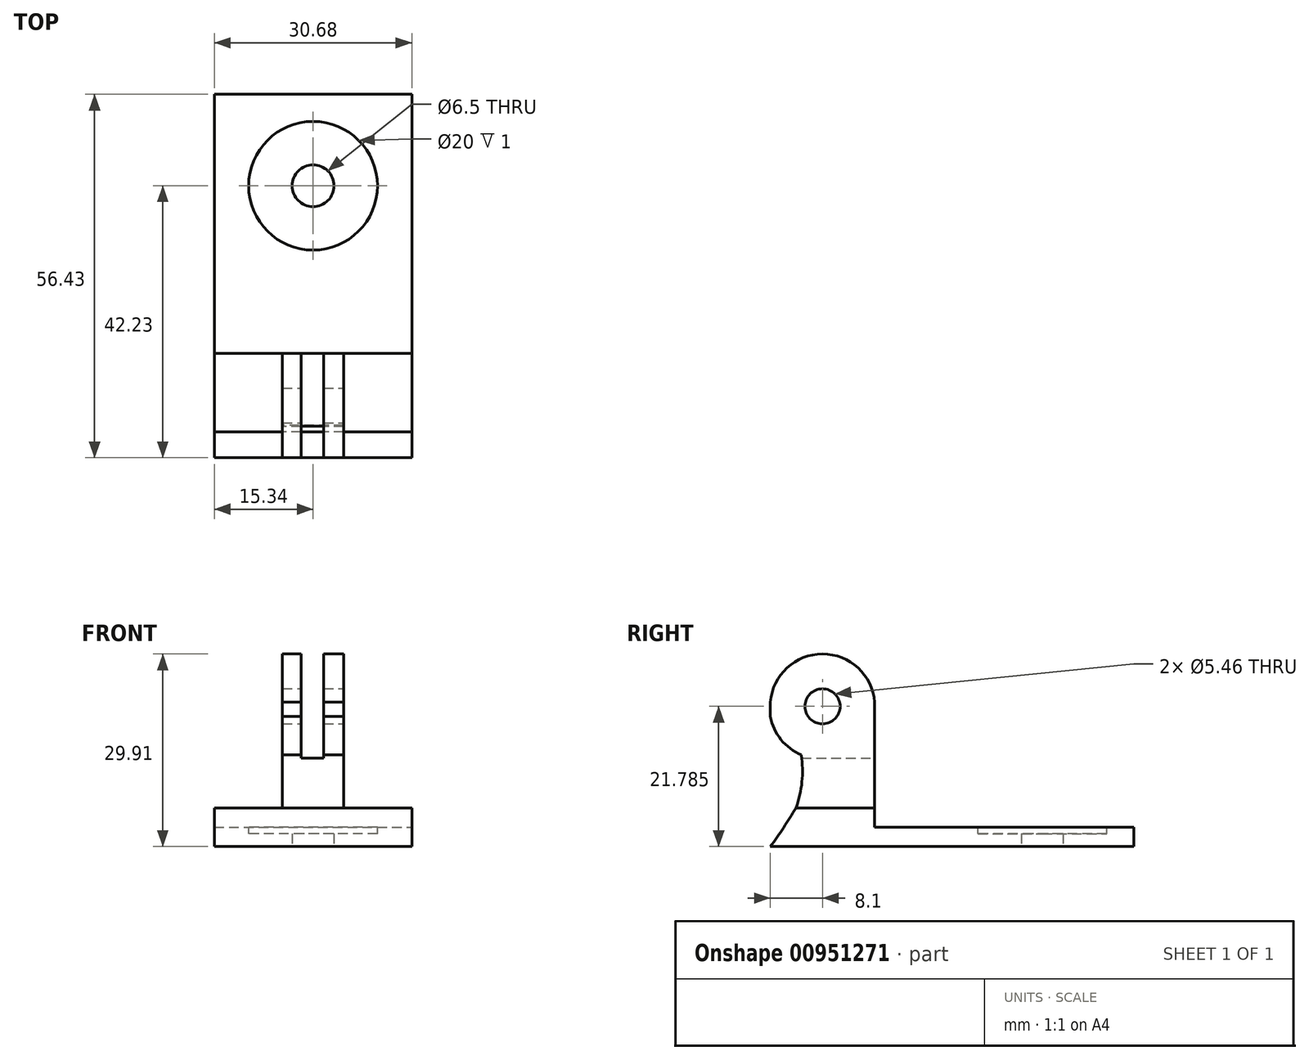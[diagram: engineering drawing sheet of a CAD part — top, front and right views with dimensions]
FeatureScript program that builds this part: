
annotation { "Feature Type Name" : "Feature", "Feature Type Description" : "" }
export const myFeature = defineFeature(function(context is Context, id is Id, definition is map)
    precondition{}
    {
        {
            var Q0;
            Q0=qCreatedBy(makeId("Top.planeOp"),FACE);
            var sketch = newSketch(context, id + "F0", { "sketchPlane" : qUnion([Q0])});
            skLineSegment(sketch, "E0.bottom", {"start": v(-15.34, 42.23) * mm, "end": v(15.34, 42.23) * mm});
            skLineSegment(sketch, "E0.top", {"start": v(-15.34, -42.23) * mm, "end": v(15.34, -42.23) * mm});
            skLineSegment(sketch, "E0.left", {"start": v(-15.34, 42.23) * mm, "end": v(-15.34, -42.23) * mm});
            skLineSegment(sketch, "E0.right", {"start": v(15.34, 42.23) * mm, "end": v(15.34, -42.23) * mm});
            skPoint(sketch, "E0.middle", {"position": v(0, 0) * mm});
            skCircle(sketch, "E1", {"center": v(0, 0) * mm, "radius": 3.25 * mm});
            skSolve(sketch);
        }
        {
            var Q0;
            Q0=makeQuery(id+"F0.imprint","IMPRINT",FACE,{"disambiguationData":[TD([[makeQuery(id+"F0.imprint","IMPRINT",EDGE,{"derivedFrom":sQuery(id+"F0.wireOp",EDGE,"E0.bottom")}),-1.0]])]});
            extrude(context, id + "F1", {"entities" : qUnion([Q0]), "depth" : 3 * mm, "offsetDistance" : 25 * mm});
        }
        {
            var Q0;
            Q0=makeQuery(id+"F1.opExtrude","CAP_FACE",FACE,{"disambiguationData":[OSD([sQuery(id+"F0.wireOp",EDGE,"E0.bottom"),sQuery(id+"F0.wireOp",EDGE,"E0.top"),sQuery(id+"F0.wireOp",EDGE,"E0.left"),sQuery(id+"F0.wireOp",EDGE,"E0.right"),sQuery(id+"F0.wireOp",EDGE,"E1")])],"isStart":false});
            var sketch = newSketch(context, id + "F2", { "sketchPlane" : qUnion([Q0])});
            skLineSegment(sketch, "E2.bottom", {"start": v(-15.34, -26.03) * mm, "end": v(15.34, -26.03) * mm});
            skLineSegment(sketch, "E2.top", {"start": v(-15.34, -42.23) * mm, "end": v(15.34, -42.23) * mm});
            skLineSegment(sketch, "E2.left", {"start": v(-15.34, -26.03) * mm, "end": v(-15.34, -42.23) * mm});
            skLineSegment(sketch, "E2.right", {"start": v(15.34, -26.03) * mm, "end": v(15.34, -42.23) * mm});
            skSolve(sketch);
        }
        {
            var Q0;
            Q0 = qSketchRegion(id + "F2", true);
            extrude(context, id + "F3", {"entities" : qUnion([Q0]), "operationType" : NewBodyOperationType.ADD, "depth" : 3 * mm, "offsetDistance" : 25 * mm});
        }
        {
            var Q0;
            Q0=makeQuery(id+"F3.opExtrude","CAP_FACE",FACE,{"disambiguationData":[OSD([sQuery(id+"F2.wireOp",EDGE,"E2.bottom"),sQuery(id+"F2.wireOp",EDGE,"E2.top"),sQuery(id+"F2.wireOp",EDGE,"E2.left"),sQuery(id+"F2.wireOp",EDGE,"E2.right")])],"isStart":false});
            var sketch = newSketch(context, id + "F4", { "sketchPlane" : qUnion([Q0])});
            skLineSegment(sketch, "E3.bottom", {"start": v(4.75, -42.23) * mm, "end": v(-4.75, -42.23) * mm});
            skLineSegment(sketch, "E3.top", {"start": v(4.75, 42.23) * mm, "end": v(-4.75, 42.23) * mm});
            skLineSegment(sketch, "E3.left", {"start": v(4.75, -42.23) * mm, "end": v(4.75, 42.23) * mm});
            skLineSegment(sketch, "E3.right", {"start": v(-4.75, -42.23) * mm, "end": v(-4.75, 42.23) * mm});
            skPoint(sketch, "E3.middle", {"position": v(0, 0) * mm});
            skLineSegment(sketch, "E4", {"start": v(-4.75, -26.03) * mm, "end": v(4.75, -26.03) * mm});
            skLineSegment(sketch, "E5", {"start": v(4.75, -26.03) * mm, "end": v(4.75, -42.23) * mm});
            skLineSegment(sketch, "E6", {"start": v(-4.75, -42.23) * mm, "end": v(-4.75, -26.03) * mm});
            skSolve(sketch);
        }
        {
            var Q0;
            {var subQ0=sQuery(id+"F4.wireOp",EDGE,"E3.bottom");Q0=makeQuery(id+"F4.imprint","IMPRINT",FACE,{"disambiguationData":[TD([[makeQuery(id+"F4.imprint","IMPRINT",EDGE,{"derivedFrom":subQ0}),1.0]])]});}
            extrude(context, id + "F5", {"entities" : qUnion([Q0]), "operationType" : NewBodyOperationType.ADD, "depth" : 24 * mm, "offsetDistance" : 25 * mm});
        }
        {
            var Q0;
            Q0=makeQuery(id+"F5.boolean.opBoolean","MERGE",FACE,{"derivedFrom":[makeQuery(id+"F3.opExtrude","SWEPT_FACE",FACE,{"disambiguationData":[OSD([sQuery(id+"F2.wireOp",EDGE,"E2.bottom")])]}),makeQuery(id+"F5.opExtrude","SWEPT_FACE",FACE,{"disambiguationData":[OSD([sQuery(id+"F4.wireOp",EDGE,"E4")])]})]});
            var sketch = newSketch(context, id + "F6", { "sketchPlane" : qUnion([Q0])});
            skLineSegment(sketch, "E7.bottom", {"start": v(-1.65, 30) * mm, "end": v(1.85, 30) * mm});
            skLineSegment(sketch, "E7.top", {"start": v(-1.65, 13.75) * mm, "end": v(1.85, 13.75) * mm});
            skLineSegment(sketch, "E7.left", {"start": v(-1.65, 30) * mm, "end": v(-1.65, 13.75) * mm});
            skLineSegment(sketch, "E7.right", {"start": v(1.85, 30) * mm, "end": v(1.85, 13.75) * mm});
            skSolve(sketch);
        }
        {
            var Q0;
            Q0=makeQuery(id+"F6.imprint","IMPRINT",FACE,{"disambiguationData":[TD([[makeQuery(id+"F6.imprint","IMPRINT",EDGE,{"derivedFrom":sQuery(id+"F6.wireOp",EDGE,"E7.bottom")}),1.0]])]});
            extrude(context, id + "F7", {"entities" : qUnion([Q0]), "operationType" : NewBodyOperationType.REMOVE, "oppositeDirection" : true, "depth" : 18 * mm, "offsetDistance" : 25 * mm});
        }
        {
            var Q0;
            Q0=makeQuery(id+"F5.opExtrude","SWEPT_FACE",FACE,{"disambiguationData":[OSD([sQuery(id+"F4.wireOp",EDGE,"E3.left")])]});
            var sketch = newSketch(context, id + "F8", { "sketchPlane" : qUnion([Q0])});
            skLineSegment(sketch, "E8", {"start": v(-34.13, 30) * mm, "end": v(-34.13, 21.78) * mm});
            skCircle(sketch, "E9", {"center": v(-34.13, 21.78) * mm, "radius": 8.13 * mm});
            skCircle(sketch, "E10", {"center": v(-34.13, 21.78) * mm, "radius": 2.73 * mm});
            skLineSegment(sketch, "E11", {"start": v(-42.23, 18) * mm, "end": v(-42.23, 30) * mm});
            skLineSegment(sketch, "E12", {"start": v(-42.23, 30) * mm, "end": v(-34.13, 30) * mm});
            skLineSegment(sketch, "E13", {"start": v(-26.03, 30) * mm, "end": v(-26.03, 22.44) * mm});
            skSolve(sketch);
        }
        {
            var Q0;
            {var subQ0=sQuery(id+"F8.wireOp",EDGE,"E12");var subQ1=sQuery(id+"F8.wireOp",EDGE,"E9");var subQ2=makeQuery(id+"F8.imprint","INTERSECT",VERTEX,{"derivedFrom":[subQ1,subQ0]});Q0=makeQuery(id+"F8.imprint","IMPRINT",FACE,{"disambiguationData":[TD([[makeQuery(id+"F8.imprint","IMPRINT",EDGE,{"disambiguationData":[TD([[subQ2,-1.0]])],"derivedFrom":subQ1}),-1.0]])]});}
            var Q1;
            {var subQ0=sQuery(id+"F8.wireOp",EDGE,"E13");Q1=makeQuery(id+"F8.imprint","IMPRINT",FACE,{"disambiguationData":[TD([[makeQuery(id+"F8.imprint","IMPRINT",EDGE,{"derivedFrom":subQ0}),-1.0]])]});}
            var Q2;
            Q2=makeQuery(id+"F8.imprint","IMPRINT",FACE,{"disambiguationData":[TD([[makeQuery(id+"F8.imprint","IMPRINT",EDGE,{"derivedFrom":sQuery(id+"F8.wireOp",EDGE,"E10")}),1.0]])]});
            extrude(context, id + "F9", {"entities" : qUnion([Q0, Q1, Q2]), "operationType" : NewBodyOperationType.REMOVE, "oppositeDirection" : true, "depth" : 10 * mm, "offsetDistance" : 25 * mm});
        }
        {
            var Q0;
            Q0=makeQuery(id+"F1.opExtrude","CAP_FACE",FACE,{"disambiguationData":[OSD([sQuery(id+"F0.wireOp",EDGE,"E0.bottom"),sQuery(id+"F0.wireOp",EDGE,"E0.top"),sQuery(id+"F0.wireOp",EDGE,"E0.left"),sQuery(id+"F0.wireOp",EDGE,"E0.right"),sQuery(id+"F0.wireOp",EDGE,"E1")])],"isStart":false});
            var sketch = newSketch(context, id + "F10", { "sketchPlane" : qUnion([Q0])});
            skCircle(sketch, "E14", {"center": v(0, 0) * mm, "radius": 10 * mm});
            skCircle(sketch, "E15", {"center": v(0, 0) * mm, "radius": 2.85 * mm});
            skSolve(sketch);
        }
        {
            var Q0;
            Q0=makeQuery(id+"F10.imprint","IMPRINT",FACE,{"disambiguationData":[TD([[makeQuery(id+"F10.imprint","IMPRINT",EDGE,{"derivedFrom":sQuery(id+"F10.wireOp",EDGE,"E14")}),1.0]])]});
            extrude(context, id + "F11", {"entities" : qUnion([Q0]), "operationType" : NewBodyOperationType.REMOVE, "oppositeDirection" : true, "depth" : 1 * mm, "offsetDistance" : 25 * mm});
        }
        {
            var Q0;
            {var subQ0=sQuery(id+"F0.wireOp",EDGE,"E0.left");var subQ1=sQuery(id+"F0.wireOp",EDGE,"E0.right");var subQ2=sQuery(id+"F0.wireOp",EDGE,"E0.bottom");Q0=makeQuery(id+"F11.boolean.opBoolean","SPLIT",FACE,{"disambiguationData":[TD([makeQuery(id+"F1.opExtrude","SWEPT_FACE",FACE,{"disambiguationData":[OSD([subQ2])]})])],"derivedFrom":makeQuery(id+"F1.opExtrude","CAP_FACE",FACE,{"disambiguationData":[OSD([subQ2,sQuery(id+"F0.wireOp",EDGE,"E0.top"),subQ0,subQ1,sQuery(id+"F0.wireOp",EDGE,"E1")])],"isStart":false})});}
            var sketch = newSketch(context, id + "F12", { "sketchPlane" : qUnion([Q0])});
            skLineSegment(sketch, "E16.bottom", {"start": v(-15.34, 42.23) * mm, "end": v(15.34, 42.23) * mm});
            skLineSegment(sketch, "E16.top", {"start": v(-15.34, 14.2) * mm, "end": v(15.34, 14.2) * mm});
            skLineSegment(sketch, "E16.left", {"start": v(-15.34, 42.23) * mm, "end": v(-15.34, 14.2) * mm});
            skLineSegment(sketch, "E16.right", {"start": v(15.34, 42.23) * mm, "end": v(15.34, 14.2) * mm});
            skSolve(sketch);
        }
        {
            var Q0;
            Q0 = qSketchRegion(id + "F12", true);
            extrude(context, id + "F13", {"entities" : qUnion([Q0]), "operationType" : NewBodyOperationType.REMOVE, "oppositeDirection" : true, "depth" : 5 * mm, "offsetDistance" : 25 * mm});
        }
        {
            var Q0;
            Q0=makeQuery(id+"F3.boolean.opBoolean","MERGE",FACE,{"derivedFrom":[makeQuery(id+"F1.opExtrude","SWEPT_FACE",FACE,{"disambiguationData":[OSD([sQuery(id+"F0.wireOp",EDGE,"E0.left")])]}),makeQuery(id+"F3.opExtrude","SWEPT_FACE",FACE,{"disambiguationData":[OSD([sQuery(id+"F2.wireOp",EDGE,"E2.left")])]})]});
            var sketch = newSketch(context, id + "F14", { "sketchPlane" : qUnion([Q0])});
            skLineSegment(sketch, "E17.0.0", {"start": v(42.23, 6) * mm, "end": v(42.23, 22.44) * mm});
            skArc(sketch, "E17.0.1", {"start": v(42.23, 22.44) * mm, "mid": v(34.13, 29.91) * mm, "end": v(26.03, 22.44) * mm});
            skLineSegment(sketch, "E17.0.2", {"start": v(26.03, 22.44) * mm, "end": v(26.03, 6) * mm});
            skLineSegment(sketch, "E17.0.3", {"start": v(26.03, 6) * mm, "end": v(42.23, 6) * mm});
            skCircle(sketch, "E18", {"center": v(34.13, 21.78) * mm, "radius": 8.25 * mm});
            skArc(sketch, "E19", {"start": v(37.43, 14.22) * mm, "mid": v(37.32, 10.06) * mm, "end": v(38.25, 6) * mm});
            skPoint(sketch, "E19.startSnap0", {"position": v(42.23, 14.22) * mm});
            skArc(sketch, "E20", {"start": v(38.25, 6) * mm, "mid": v(40.17, 2.95) * mm, "end": v(42.23, 0) * mm});
            skSolve(sketch);
        }
        {
            var Q0;
            {var subQ5=sQuery(id+"F14.wireOp",EDGE,"E19");Q0=makeQuery(id+"F14.imprint","IMPRINT",FACE,{"disambiguationData":[TD([[makeQuery(id+"F14.imprint","IMPRINT",EDGE,{"derivedFrom":subQ5}),1.0]])]});}
            var Q1;
            {var subQ2=sQuery(id+"F14.wireOp",EDGE,"E20");Q1=makeQuery(id+"F14.imprint","IMPRINT",FACE,{"disambiguationData":[TD([[makeQuery(id+"F14.imprint","IMPRINT",EDGE,{"derivedFrom":subQ2}),1.0]])]});}
            extrude(context, id + "F15", {"entities" : qUnion([Q0, Q1]), "operationType" : NewBodyOperationType.REMOVE, "endBound" : BoundingType.THROUGH_ALL, "oppositeDirection" : true, "depth" : 25 * mm, "offsetDistance" : 25 * mm});
        }
    });
